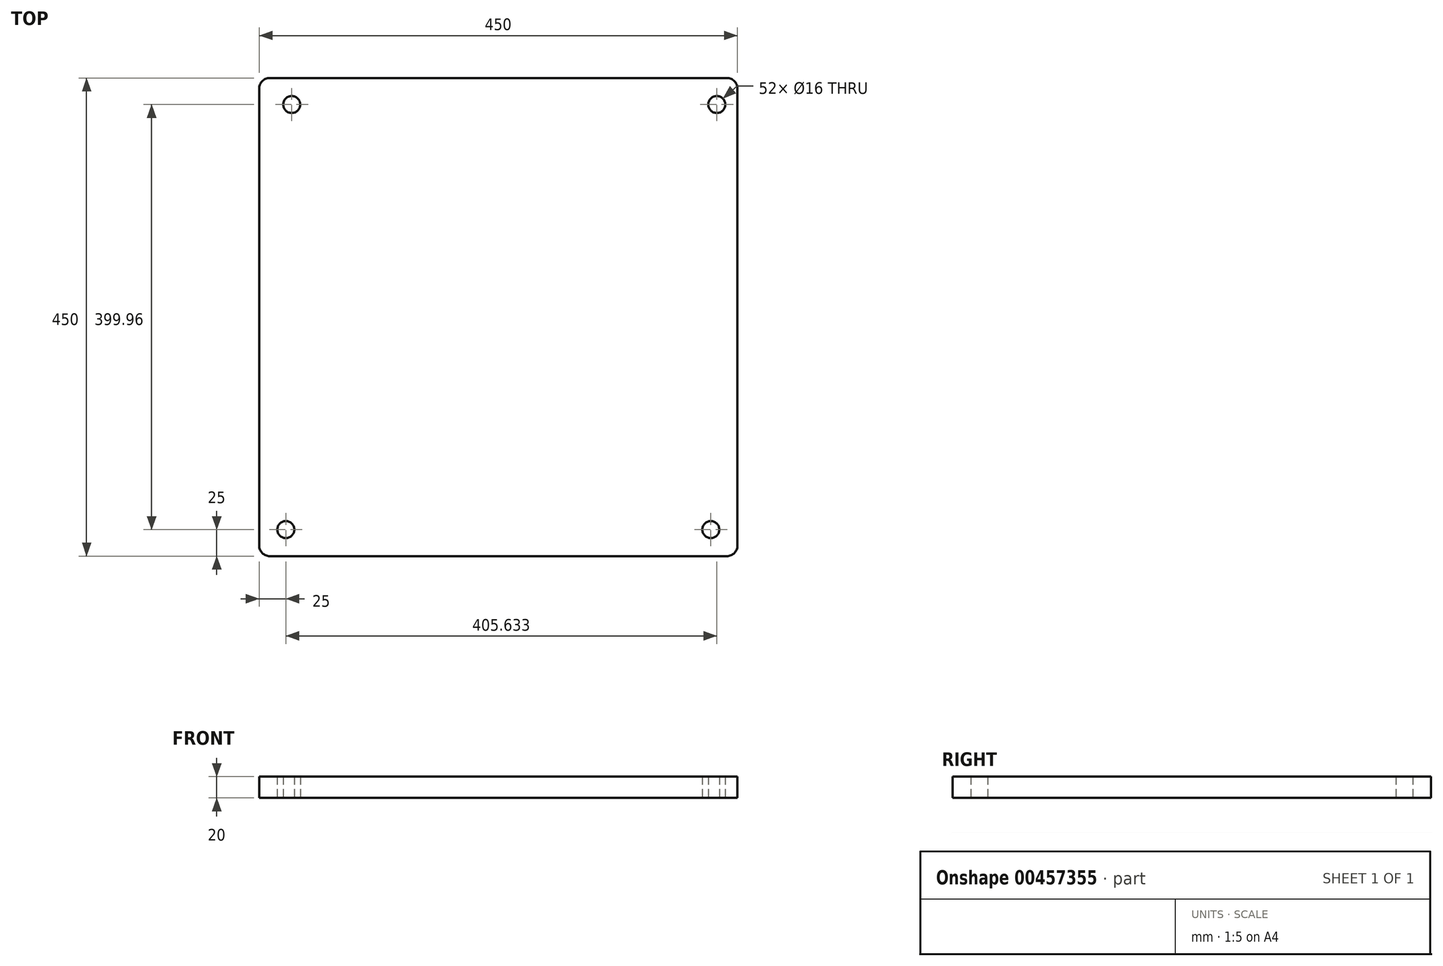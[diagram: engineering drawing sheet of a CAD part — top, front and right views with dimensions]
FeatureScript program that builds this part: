
annotation { "Feature Type Name" : "Feature", "Feature Type Description" : "" }
export const myFeature = defineFeature(function(context is Context, id is Id, definition is map)
    precondition{}
    {
        {
            var Q0;
            Q0=qCreatedBy(makeId("Top.planeOp"),FACE);
            var sketch = newSketch(context, id + "F0", { "sketchPlane" : qUnion([Q0])});
            skLineSegment(sketch, "E0.bottom", {"start": v(0, 0) * mm, "end": v(450, 0) * mm});
            skLineSegment(sketch, "E0.top", {"start": v(0, 450) * mm, "end": v(450, 450) * mm});
            skLineSegment(sketch, "E0.left", {"start": v(0, 0) * mm, "end": v(0, 450) * mm});
            skLineSegment(sketch, "E0.right", {"start": v(450, 0) * mm, "end": v(450, 450) * mm});
            skCircle(sketch, "E1", {"center": v(25, 25) * mm, "radius": 8 * mm});
            skCircle(sketch, "E2.0.1.0", {"center": v(30.63, 424.96) * mm, "radius": 8 * mm});
            skCircle(sketch, "E2.1.0.0", {"center": v(425, 25) * mm, "radius": 8 * mm});
            skCircle(sketch, "E2.1.1.0", {"center": v(430.63, 424.96) * mm, "radius": 8 * mm});
            skLineSegment(sketch, "E2.direction1", {"start": v(25, 25) * mm, "end": v(425, 25) * mm, "construction": true});
            skLineSegment(sketch, "E2.direction2", {"start": v(25, 25) * mm, "end": v(30.63, 424.96) * mm, "construction": true});
            skSolve(sketch);
        }
        {
            var Q0;
            Q0=makeQuery(id+"F0.imprint","IMPRINT",FACE,{"disambiguationData":[TD([[makeQuery(id+"F0.imprint","IMPRINT",EDGE,{"derivedFrom":sQuery(id+"F0.wireOp",EDGE,"E0.bottom")}),1.0]])]});
            extrude(context, id + "F1", {"entities" : qUnion([Q0]), "depth" : 20 * mm});
        }
        {
            var Q0;
            Q0=makeQuery(id+"F1.opExtrude","SWEPT_EDGE",EDGE,{"disambiguationData":[OSD([sQuery(id+"F0.wireOp",EDGE,"E0.bottom"),sQuery(id+"F0.wireOp",EDGE,"E0.left")])]});
            var Q1;
            Q1=makeQuery(id+"F1.opExtrude","SWEPT_EDGE",EDGE,{"disambiguationData":[OSD([sQuery(id+"F0.wireOp",EDGE,"E0.bottom"),sQuery(id+"F0.wireOp",EDGE,"E0.right")])]});
            var Q2;
            Q2=makeQuery(id+"F1.opExtrude","SWEPT_EDGE",EDGE,{"disambiguationData":[OSD([sQuery(id+"F0.wireOp",EDGE,"E0.top"),sQuery(id+"F0.wireOp",EDGE,"E0.right")])]});
            var Q3;
            Q3=makeQuery(id+"F1.opExtrude","SWEPT_EDGE",EDGE,{"disambiguationData":[OSD([sQuery(id+"F0.wireOp",EDGE,"E0.top"),sQuery(id+"F0.wireOp",EDGE,"E0.left")])]});
            fillet(context, id + "F2", {"entities" : qUnion([Q0, Q1, Q2, Q3]), "radius" : 10 * mm, "tangentPropagation" : true, "allowEdgeOverflow" : false});
        }
    });
